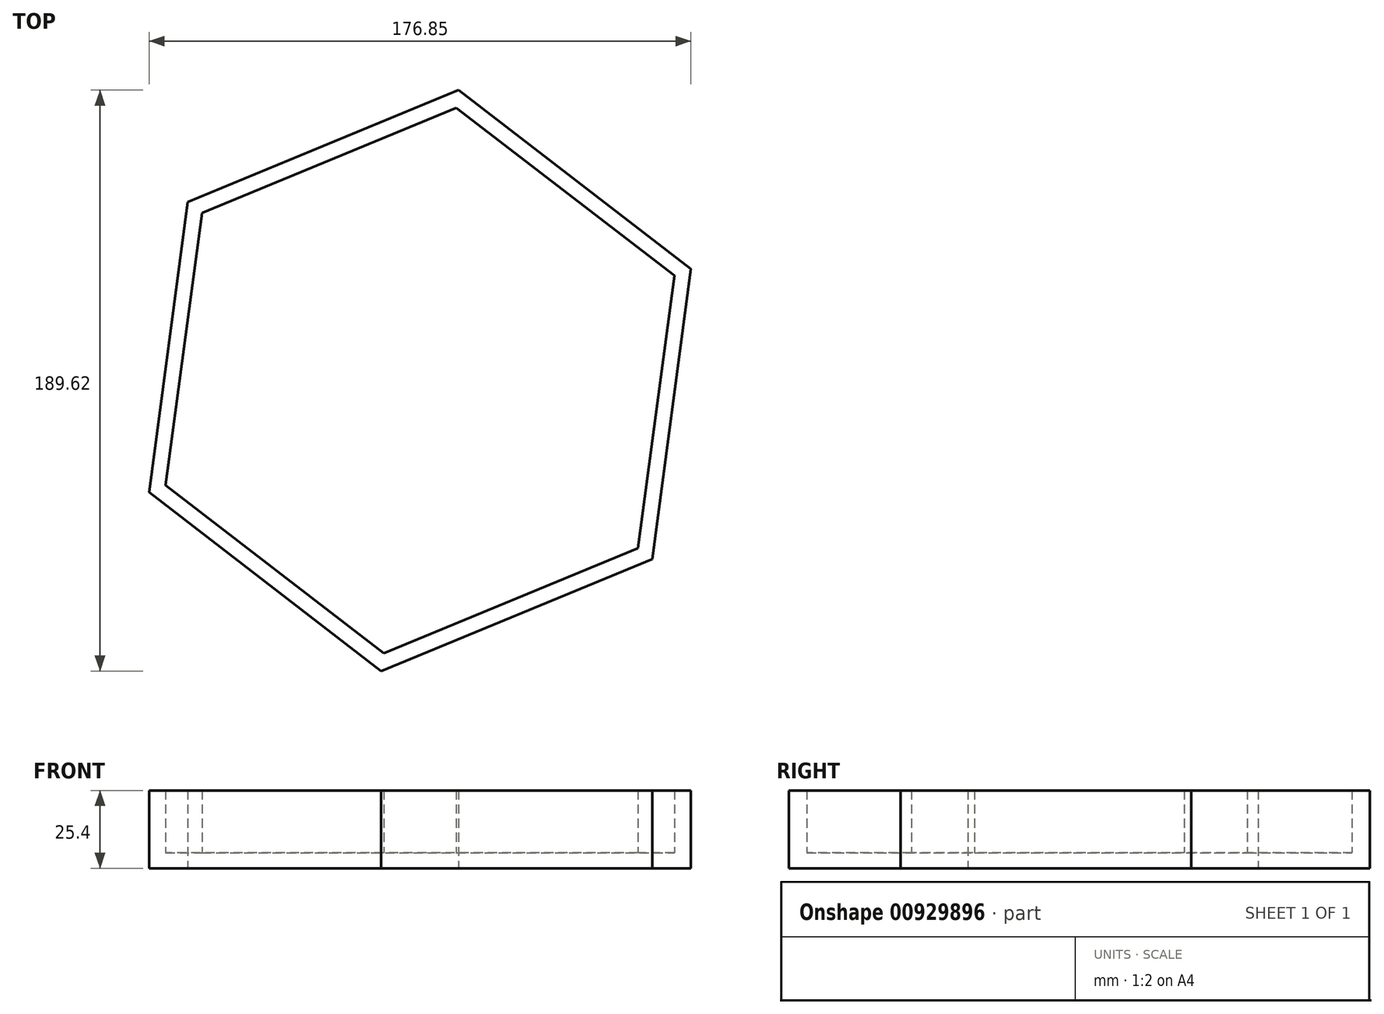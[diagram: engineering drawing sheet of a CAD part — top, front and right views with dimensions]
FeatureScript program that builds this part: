
annotation { "Feature Type Name" : "Feature", "Feature Type Description" : "" }
export const myFeature = defineFeature(function(context is Context, id is Id, definition is map)
    precondition{}
    {
        {
            var Q0;
            Q0=qCreatedBy(makeId("Top.planeOp"),FACE);
            var sketch = newSketch(context, id + "F0", { "sketchPlane" : qUnion([Q0])});
            skCircle(sketch, "E0.cCircle", {"center": v(8.94, 0) * mm, "radius": 82.84 * mm, "construction": true});
            skLineSegment(sketch, "E0.0", {"start": v(97.37, 36.46) * mm, "end": v(84.74, -58.35) * mm});
            skLineSegment(sketch, "E0.1", {"start": v(84.74, -58.35) * mm, "end": v(-3.7, -94.81) * mm});
            skLineSegment(sketch, "E0.2", {"start": v(-3.7, -94.81) * mm, "end": v(-79.48, -36.46) * mm});
            skLineSegment(sketch, "E0.3", {"start": v(-79.48, -36.46) * mm, "end": v(-66.85, 58.35) * mm});
            skLineSegment(sketch, "E0.4", {"start": v(-66.85, 58.35) * mm, "end": v(21.58, 94.81) * mm});
            skLineSegment(sketch, "E0.5", {"start": v(21.58, 94.81) * mm, "end": v(97.37, 36.46) * mm});
            skPoint(sketch, "E0.0.midPoint", {"position": v(91.05, -10.94) * mm});
            skSolve(sketch);
        }
        {
            var Q0;
            Q0 = qSketchRegion(id + "F0", true);
            var Q1;
            Q1=makeQuery(id+"F0.imprint","IMPRINT",FACE,{"disambiguationData":[TD([[makeQuery(id+"F0.imprint","IMPRINT",EDGE,{"derivedFrom":sQuery(id+"F0.wireOp",EDGE,"E0.0")}),-1.0]])]});
            extrude(context, id + "F1", {"entities" : qUnion([Q0, Q1]), "depth" : 25.4 * mm, "offsetDistance" : 25.4 * mm});
        }
        {
            var Q0;
            Q0=makeQuery(id+"F1.opExtrude","CAP_FACE",FACE,{"disambiguationData":[OSD([sQuery(id+"F0.wireOp",EDGE,"E0.0"),sQuery(id+"F0.wireOp",EDGE,"E0.1"),sQuery(id+"F0.wireOp",EDGE,"E0.2"),sQuery(id+"F0.wireOp",EDGE,"E0.3"),sQuery(id+"F0.wireOp",EDGE,"E0.4"),sQuery(id+"F0.wireOp",EDGE,"E0.5")])],"isStart":false});
            shell(context, id + "F2", {"entities" : qUnion([Q0]), "thickness" : 5.08 * mm});
        }
    });
